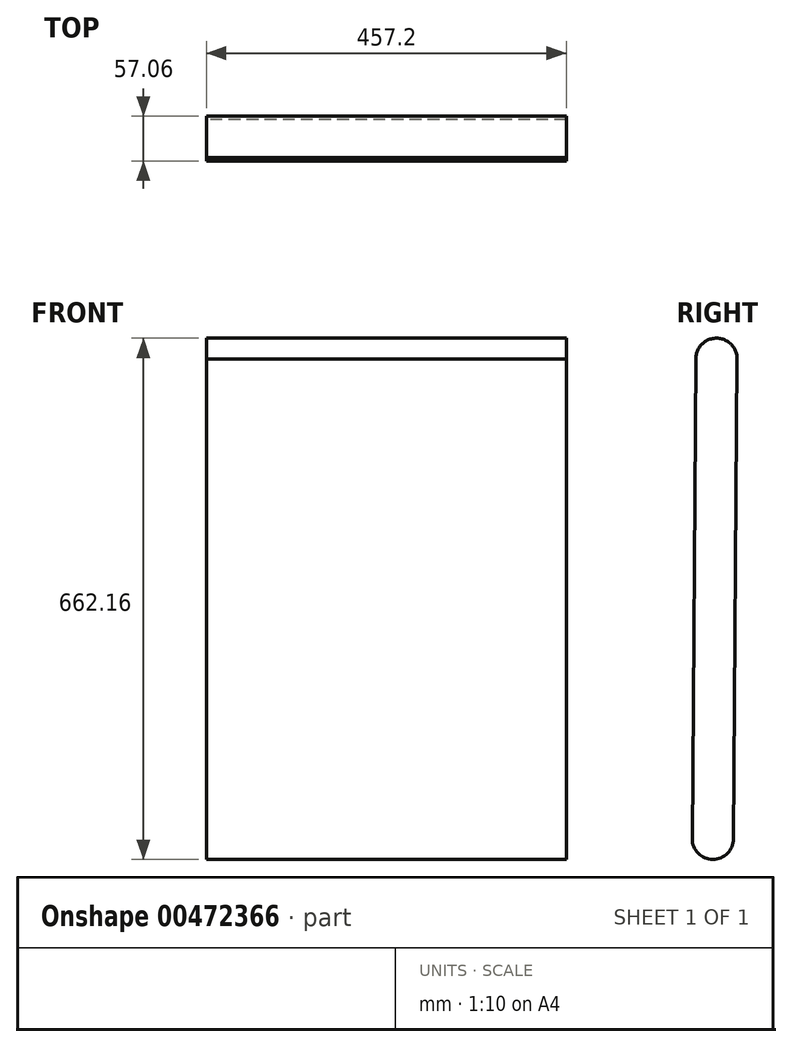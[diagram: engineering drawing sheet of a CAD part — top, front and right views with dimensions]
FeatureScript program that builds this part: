
annotation { "Feature Type Name" : "Feature", "Feature Type Description" : "" }
export const myFeature = defineFeature(function(context is Context, id is Id, definition is map)
    precondition{}
    {
        {
            var Q0;
            Q0=qCreatedBy(makeId("Right.planeOp"),FACE);
            var sketch = newSketch(context, id + "F0", { "sketchPlane" : qUnion([Q0])});
            skCircle(sketch, "E0", {"center": v(-5.49, 47.9) * mm, "radius": 26.19 * mm});
            skCircle(sketch, "E1", {"center": v(-10.17, -561.88) * mm, "radius": 26.19 * mm});
            skLineSegment(sketch, "E2", {"start": v(16.02, -561.88) * mm, "end": v(20.7, 47.7) * mm});
            skLineSegment(sketch, "E3", {"start": v(-36.36, -561.88) * mm, "end": v(-31.68, 47.82) * mm});
            skSolve(sketch);
        }
        {
            var Q0;
            {var subQ0=sQuery(id+"F0.wireOp",EDGE,"E2");Q0=makeQuery(id+"F0.imprint","IMPRINT",FACE,{"disambiguationData":[TD([[makeQuery(id+"F0.imprint","IMPRINT",EDGE,{"derivedFrom":subQ0}),1.0]])]});}
            var Q1;
            {var subQ0=sQuery(id+"F0.wireOp",EDGE,"E1");var subQ1=makeQuery(id+"F0.imprint","INTERSECT",VERTEX,{"derivedFrom":[subQ0,sQuery(id+"F0.wireOp",EDGE,"E2")]});Q1=makeQuery(id+"F0.imprint","IMPRINT",FACE,{"disambiguationData":[TD([[makeQuery(id+"F0.imprint","IMPRINT",EDGE,{"disambiguationData":[TD([[subQ1,-1.0]])],"derivedFrom":subQ0}),1.0]])]});}
            var Q2;
            {var subQ0=sQuery(id+"F0.wireOp",EDGE,"E0");var subQ1=makeQuery(id+"F0.imprint","INTERSECT",VERTEX,{"derivedFrom":[subQ0,sQuery(id+"F0.wireOp",EDGE,"E2")]});Q2=makeQuery(id+"F0.imprint","IMPRINT",FACE,{"disambiguationData":[TD([[makeQuery(id+"F0.imprint","IMPRINT",EDGE,{"disambiguationData":[TD([[subQ1,1.0]])],"derivedFrom":subQ0}),1.0]])]});}
            extrude(context, id + "F1", {"entities" : qUnion([Q0, Q1, Q2]), "depth" : 457.2 * mm});
        }
    });
